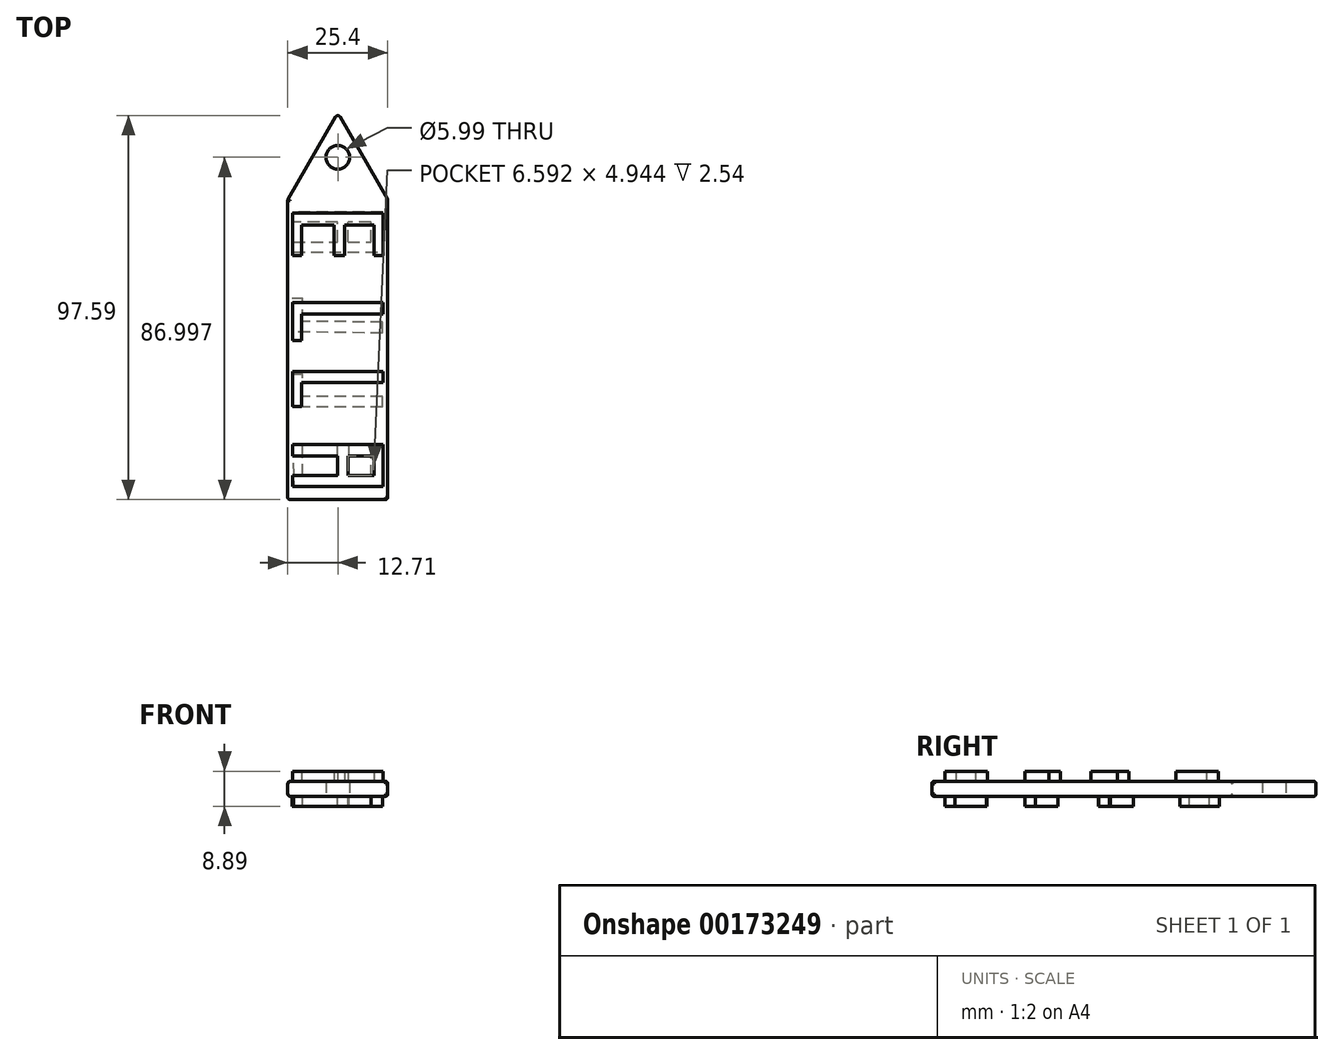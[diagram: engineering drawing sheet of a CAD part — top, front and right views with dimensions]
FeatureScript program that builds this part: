
annotation { "Feature Type Name" : "Feature", "Feature Type Description" : "" }
export const myFeature = defineFeature(function(context is Context, id is Id, definition is map)
    precondition{}
    {
        {
            var Q0;
            Q0=qCreatedBy(makeId("Top.planeOp"),FACE);
            var sketch = newSketch(context, id + "F0", { "sketchPlane" : qUnion([Q0])});
            skLineSegment(sketch, "E0.top", {"start": v(-25.4, -45.22) * mm, "end": v(0, -45.22) * mm});
            skLineSegment(sketch, "E0.left", {"start": v(-25.4, 30.98) * mm, "end": v(-25.4, -45.22) * mm});
            skLineSegment(sketch, "E0.right", {"start": v(0, 30.98) * mm, "end": v(0, -45.22) * mm});
            skLineSegment(sketch, "E1.1", {"start": v(-25.4, 30.98) * mm, "end": v(-12.7, 52.98) * mm});
            skLineSegment(sketch, "E1.2", {"start": v(-12.7, 52.98) * mm, "end": v(0, 30.98) * mm});
            skPoint(sketch, "E1.0.midPoint", {"position": v(-12.7, 30.98) * mm});
            skCircle(sketch, "E2", {"center": v(-12.69, 41.78) * mm, "radius": 3 * mm});
            skSolve(sketch);
        }
        {
            var Q0;
            Q0 = qSketchRegion(id + "F0", true);
            extrude(context, id + "F1", {"entities" : qUnion([Q0]), "depth" : 3.8 * mm});
        }
        {
            var Q0;
            Q0=makeQuery(id+"F1.opExtrude","CAP_FACE",FACE,{"disambiguationData":[OSD([sQuery(id+"F0.wireOp",EDGE,"E0.top"),sQuery(id+"F0.wireOp",EDGE,"E0.left"),sQuery(id+"F0.wireOp",EDGE,"E0.right"),sQuery(id+"F0.wireOp",EDGE,"E1.1"),sQuery(id+"F0.wireOp",EDGE,"E1.2"),sQuery(id+"F0.wireOp",EDGE,"E2")])],"isStart":false});
            var sketch = newSketch(context, id + "F2", { "sketchPlane" : qUnion([Q0])});
            skLineSegment(sketch, "E3.bottom", {"start": v(-3.54, 24.54) * mm, "end": v(-10.96, 24.54) * mm});
            skLineSegment(sketch, "E3.top", {"start": v(-1.15, 27.6) * mm, "end": v(-24.22, 27.6) * mm});
            skLineSegment(sketch, "E3.left", {"start": v(-1.15, 24.54) * mm, "end": v(-1.15, 27.6) * mm});
            skLineSegment(sketch, "E3.right", {"start": v(-24.22, 24.54) * mm, "end": v(-24.22, 27.6) * mm});
            skLineSegment(sketch, "E4.bottom", {"start": v(-1.15, 27.6) * mm, "end": v(-3.54, 27.6) * mm});
            skLineSegment(sketch, "E4.top", {"start": v(-1.15, 16.8) * mm, "end": v(-3.54, 16.8) * mm});
            skLineSegment(sketch, "E4.left", {"start": v(-1.15, 27.6) * mm, "end": v(-1.15, 16.8) * mm});
            skLineSegment(sketch, "E4.right", {"start": v(-3.54, 24.54) * mm, "end": v(-3.54, 16.8) * mm});
            skLineSegment(sketch, "E5.bottom", {"start": v(-10.96, 27.6) * mm, "end": v(-13.6, 27.6) * mm});
            skLineSegment(sketch, "E5.top", {"start": v(-10.96, 16.8) * mm, "end": v(-13.6, 16.8) * mm});
            skLineSegment(sketch, "E5.left", {"start": v(-13.6, 24.54) * mm, "end": v(-13.6, 16.8) * mm});
            skLineSegment(sketch, "E5.right", {"start": v(-10.96, 24.54) * mm, "end": v(-10.96, 16.8) * mm});
            skLineSegment(sketch, "E6.bottom", {"start": v(-24.22, 27.6) * mm, "end": v(-21.91, 27.6) * mm});
            skLineSegment(sketch, "E6.top", {"start": v(-24.22, 16.8) * mm, "end": v(-21.91, 16.8) * mm});
            skLineSegment(sketch, "E6.left", {"start": v(-24.22, 27.6) * mm, "end": v(-24.22, 16.8) * mm});
            skLineSegment(sketch, "E6.right", {"start": v(-21.91, 24.54) * mm, "end": v(-21.91, 16.8) * mm});
            skLineSegment(sketch, "E7.bottom", {"start": v(-1.15, 1.96) * mm, "end": v(-21.91, 1.96) * mm});
            skLineSegment(sketch, "E7.top", {"start": v(-1.15, 4.85) * mm, "end": v(-24.22, 4.85) * mm});
            skLineSegment(sketch, "E7.left", {"start": v(-1.15, 4.85) * mm, "end": v(-1.15, 1.96) * mm});
            skLineSegment(sketch, "E7.right", {"start": v(-24.22, 4.85) * mm, "end": v(-24.22, 1.96) * mm});
            skLineSegment(sketch, "E8.top", {"start": v(-24.22, -4.8) * mm, "end": v(-21.91, -4.8) * mm});
            skLineSegment(sketch, "E8.left", {"start": v(-24.22, 1.96) * mm, "end": v(-24.22, -4.8) * mm});
            skLineSegment(sketch, "E8.right", {"start": v(-21.91, 1.96) * mm, "end": v(-21.91, -4.8) * mm});
            skLineSegment(sketch, "E9.bottom", {"start": v(-1.15, -12.62) * mm, "end": v(-24.22, -12.62) * mm});
            skLineSegment(sketch, "E9.top", {"start": v(-1.15, -15.5) * mm, "end": v(-21.91, -15.5) * mm});
            skLineSegment(sketch, "E9.left", {"start": v(-1.15, -12.62) * mm, "end": v(-1.15, -15.5) * mm});
            skLineSegment(sketch, "E9.right", {"start": v(-24.22, -12.62) * mm, "end": v(-24.22, -15.5) * mm});
            skLineSegment(sketch, "E10.bottom", {"start": v(-24.22, -12.62) * mm, "end": v(-21.91, -12.62) * mm});
            skLineSegment(sketch, "E10.top", {"start": v(-24.22, -21.6) * mm, "end": v(-21.91, -21.6) * mm});
            skLineSegment(sketch, "E10.left", {"start": v(-24.22, -12.62) * mm, "end": v(-24.22, -21.6) * mm});
            skLineSegment(sketch, "E10.right", {"start": v(-21.91, -15.5) * mm, "end": v(-21.91, -21.6) * mm});
            skLineSegment(sketch, "E11.bottom", {"start": v(-24.22, -31.16) * mm, "end": v(-1.15, -31.16) * mm});
            skLineSegment(sketch, "E11.top", {"start": v(-24.22, -34.13) * mm, "end": v(-12.7, -34.13) * mm});
            skLineSegment(sketch, "E11.left", {"start": v(-24.22, -31.16) * mm, "end": v(-24.22, -34.13) * mm});
            skLineSegment(sketch, "E11.right", {"start": v(-1.15, -31.16) * mm, "end": v(-1.15, -34.13) * mm});
            skLineSegment(sketch, "E12.bottom", {"start": v(-1.15, -31.16) * mm, "end": v(-3.54, -31.16) * mm});
            skLineSegment(sketch, "E12.top", {"start": v(-1.15, -41.87) * mm, "end": v(-3.54, -41.87) * mm});
            skLineSegment(sketch, "E12.left", {"start": v(-1.15, -31.16) * mm, "end": v(-1.15, -41.87) * mm});
            skLineSegment(sketch, "E12.right", {"start": v(-3.54, -34.13) * mm, "end": v(-3.54, -39.07) * mm});
            skLineSegment(sketch, "E13.bottom", {"start": v(-1.15, -41.87) * mm, "end": v(-24.22, -41.87) * mm});
            skLineSegment(sketch, "E13.top", {"start": v(-3.54, -39.07) * mm, "end": v(-10.13, -39.07) * mm});
            skLineSegment(sketch, "E13.left", {"start": v(-1.15, -41.87) * mm, "end": v(-1.15, -39.07) * mm});
            skLineSegment(sketch, "E13.right", {"start": v(-24.22, -41.87) * mm, "end": v(-24.22, -39.07) * mm});
            skLineSegment(sketch, "E14.bottom", {"start": v(-12.7, -31.16) * mm, "end": v(-10.13, -31.16) * mm});
            skLineSegment(sketch, "E14.top", {"start": v(-12.7, -41.87) * mm, "end": v(-10.13, -41.87) * mm});
            skLineSegment(sketch, "E14.left", {"start": v(-12.7, -34.13) * mm, "end": v(-12.7, -39.07) * mm});
            skLineSegment(sketch, "E14.right", {"start": v(-10.13, -34.13) * mm, "end": v(-10.13, -39.07) * mm});
            skLineSegment(sketch, "E15.trimOffspring", {"start": v(-13.6, 24.54) * mm, "end": v(-21.91, 24.54) * mm});
            skLineSegment(sketch, "E16.trimOffspring", {"start": v(-10.13, -34.13) * mm, "end": v(-3.54, -34.13) * mm});
            skLineSegment(sketch, "E17.trimOffspring", {"start": v(-12.7, -39.07) * mm, "end": v(-24.22, -39.07) * mm});
            skSolve(sketch);
        }
        {
            var Q0;
            Q0 = qSketchRegion(id + "F2", true);
            extrude(context, id + "F3", {"entities" : qUnion([Q0]), "operationType" : NewBodyOperationType.ADD, "depth" : 2.54 * mm});
        }
        {
            var Q0;
            Q0=makeQuery(id+"F1.opExtrude","SWEPT_FACE",FACE,{"disambiguationData":[OSD([sQuery(id+"F0.wireOp",EDGE,"E0.left")])]});
            fillet(context, id + "F4", {"entities" : qUnion([Q0]), "radius" : 0.61 * mm, "tangentPropagation" : true, "allowEdgeOverflow" : false});
        }
        {
            var Q0;
            Q0=makeQuery(id+"F1.opExtrude","SWEPT_FACE",FACE,{"disambiguationData":[OSD([sQuery(id+"F0.wireOp",EDGE,"E0.top")])]});
            fillet(context, id + "F5", {"entities" : qUnion([Q0]), "radius" : 0.61 * mm, "tangentPropagation" : true, "allowEdgeOverflow" : false});
        }
        {
            var Q0;
            Q0=makeQuery(id+"F1.opExtrude","SWEPT_FACE",FACE,{"disambiguationData":[OSD([sQuery(id+"F0.wireOp",EDGE,"E1.1")])]});
            fillet(context, id + "F6", {"entities" : qUnion([Q0]), "radius" : 0.6 * mm, "tangentPropagation" : true, "allowEdgeOverflow" : false});
        }
        {
            var Q0;
            Q0=makeQuery(id+"F1.opExtrude","SWEPT_FACE",FACE,{"disambiguationData":[OSD([sQuery(id+"F0.wireOp",EDGE,"E0.right")])]});
            fillet(context, id + "F7", {"entities" : qUnion([Q0]), "radius" : 0.6 * mm, "tangentPropagation" : true, "allowEdgeOverflow" : false});
        }
        {
            var Q0;
            Q0=makeQuery(id+"F1.opExtrude","SWEPT_FACE",FACE,{"disambiguationData":[OSD([sQuery(id+"F0.wireOp",EDGE,"E1.2")])]});
            fillet(context, id + "F8", {"entities" : qUnion([Q0]), "radius" : 0.6 * mm, "tangentPropagation" : true, "allowEdgeOverflow" : false});
        }
        {
            var Q0;
            Q0=makeQuery(id+"F1.opExtrude","CAP_FACE",FACE,{"disambiguationData":[OSD([sQuery(id+"F0.wireOp",EDGE,"E0.top"),sQuery(id+"F0.wireOp",EDGE,"E0.left"),sQuery(id+"F0.wireOp",EDGE,"E0.right"),sQuery(id+"F0.wireOp",EDGE,"E1.1"),sQuery(id+"F0.wireOp",EDGE,"E1.2"),sQuery(id+"F0.wireOp",EDGE,"E2")])],"isStart":true});
            var sketch = newSketch(context, id + "F9", { "sketchPlane" : qUnion([Q0])});
            skLineSegment(sketch, "E18.left", {"start": v(-1.34, 41.86) * mm, "end": v(-1.32, 39.4) * mm});
            skLineSegment(sketch, "E19.bottom", {"start": v(-1.34, 41.86) * mm, "end": v(-4.2, 41.86) * mm});
            skLineSegment(sketch, "E19.top", {"start": v(-1.34, 31.33) * mm, "end": v(-4.2, 31.33) * mm});
            skLineSegment(sketch, "E19.left", {"start": v(-1.34, 41.86) * mm, "end": v(-1.34, 31.33) * mm});
            skLineSegment(sketch, "E19.right", {"start": v(-4.2, 41.86) * mm, "end": v(-4.2, 31.33) * mm});
            skLineSegment(sketch, "E20.bottom", {"start": v(-9.8, 41.7) * mm, "end": v(-12.77, 41.7) * mm});
            skLineSegment(sketch, "E20.top", {"start": v(-9.8, 31.25) * mm, "end": v(-12.77, 31.25) * mm});
            skLineSegment(sketch, "E20.left", {"start": v(-9.8, 41.7) * mm, "end": v(-9.8, 31.25) * mm});
            skLineSegment(sketch, "E20.right", {"start": v(-12.77, 41.7) * mm, "end": v(-12.77, 31.25) * mm});
            skLineSegment(sketch, "E21.right", {"start": v(-21.63, 41.86) * mm, "end": v(-21.63, 31.25) * mm});
            skLineSegment(sketch, "E22.bottom", {"start": v(-1.34, 21.62) * mm, "end": v(-24.19, 21.62) * mm});
            skLineSegment(sketch, "E22.top", {"start": v(-1.34, 18.95) * mm, "end": v(-24.19, 18.95) * mm});
            skLineSegment(sketch, "E22.left", {"start": v(-1.34, 21.62) * mm, "end": v(-1.34, 18.95) * mm});
            skLineSegment(sketch, "E23.right", {"start": v(-21.71, 21.62) * mm, "end": v(-21.63, 13.24) * mm});
            skLineSegment(sketch, "E24.bottom", {"start": v(-1.34, 2.87) * mm, "end": v(-24.31, 2.6) * mm});
            skLineSegment(sketch, "E24.left", {"start": v(-1.34, 2.87) * mm, "end": v(-1.34, 0.1) * mm});
            skLineSegment(sketch, "E25.bottom", {"start": v(-24.31, 2.6) * mm, "end": v(-21.72, 2.6) * mm});
            skLineSegment(sketch, "E25.top", {"start": v(-24.31, -5.96) * mm, "end": v(-21.63, -5.96) * mm});
            skLineSegment(sketch, "E25.right", {"start": v(-21.72, 2.6) * mm, "end": v(-21.63, -5.96) * mm});
            skLineSegment(sketch, "E26.bottom", {"start": v(-24.03, -17.73) * mm, "end": v(-1.31, -17.73) * mm});
            skLineSegment(sketch, "E26.top", {"start": v(-24.06, -20.24) * mm, "end": v(-1.34, -20.24) * mm});
            skLineSegment(sketch, "E26.right", {"start": v(-1.31, -17.73) * mm, "end": v(-1.34, -20.24) * mm});
            skLineSegment(sketch, "E27.bottom", {"start": v(-1.31, -17.73) * mm, "end": v(-4.28, -17.73) * mm});
            skLineSegment(sketch, "E27.top", {"start": v(-1.31, -27.88) * mm, "end": v(-4.28, -27.88) * mm});
            skLineSegment(sketch, "E27.left", {"start": v(-1.31, -17.73) * mm, "end": v(-1.31, -27.88) * mm});
            skLineSegment(sketch, "E27.right", {"start": v(-4.28, -17.73) * mm, "end": v(-4.28, -27.88) * mm});
            skLineSegment(sketch, "E28.bottom", {"start": v(-1.31, -27.88) * mm, "end": v(-24.07, -27.88) * mm});
            skLineSegment(sketch, "E28.top", {"start": v(-1.31, -25.3) * mm, "end": v(-24.07, -25.3) * mm});
            skLineSegment(sketch, "E28.left", {"start": v(-1.31, -27.88) * mm, "end": v(-1.31, -25.3) * mm});
            skLineSegment(sketch, "E29.bottom", {"start": v(-10.13, -17.73) * mm, "end": v(-12.77, -17.73) * mm});
            skLineSegment(sketch, "E29.top", {"start": v(-10.13, -27.88) * mm, "end": v(-12.77, -27.88) * mm});
            skLineSegment(sketch, "E29.left", {"start": v(-10.13, -17.73) * mm, "end": v(-10.13, -27.88) * mm});
            skLineSegment(sketch, "E29.right", {"start": v(-12.77, -17.73) * mm, "end": v(-12.77, -27.88) * mm});
            skLineSegment(sketch, "E30", {"start": v(-1.34, 41.86) * mm, "end": v(-23.94, 41.7) * mm});
            skPoint(sketch, "E30.endSnap0", {"position": v(-11.29, 41.7) * mm});
            skLineSegment(sketch, "E31", {"start": v(-21.63, 31.25) * mm, "end": v(-24.11, 31.25) * mm});
            skLineSegment(sketch, "E32", {"start": v(-24.11, 31.25) * mm, "end": v(-23.94, 41.7) * mm});
            skLineSegment(sketch, "E33", {"start": v(-1.32, 39.4) * mm, "end": v(-23.98, 39.17) * mm});
            skLineSegment(sketch, "E34", {"start": v(-24.19, 21.62) * mm, "end": v(-24.19, 13.24) * mm});
            skLineSegment(sketch, "E35", {"start": v(-24.19, 13.24) * mm, "end": v(-21.63, 13.24) * mm});
            skLineSegment(sketch, "E36", {"start": v(-24.31, 2.6) * mm, "end": v(-24.31, -5.96) * mm});
            skLineSegment(sketch, "E37", {"start": v(-24.03, -17.73) * mm, "end": v(-24.06, -20.24) * mm});
            skLineSegment(sketch, "E38", {"start": v(-24.07, -25.3) * mm, "end": v(-24.07, -27.88) * mm});
            skLineSegment(sketch, "E39", {"start": v(-1.34, 0.1) * mm, "end": v(-23.02, -0.12) * mm});
            skPoint(sketch, "E39.endSnap0", {"position": v(-23.02, 2.6) * mm});
            skLineSegment(sketch, "E40", {"start": v(-23.02, -0.12) * mm, "end": v(-1.34, 0.1) * mm});
            skSolve(sketch);
        }
        {
            var Q0;
            Q0 = qSketchRegion(id + "F9", true);
            extrude(context, id + "F10", {"entities" : qUnion([Q0]), "operationType" : NewBodyOperationType.ADD, "depth" : 2.54 * mm});
        }
    });
